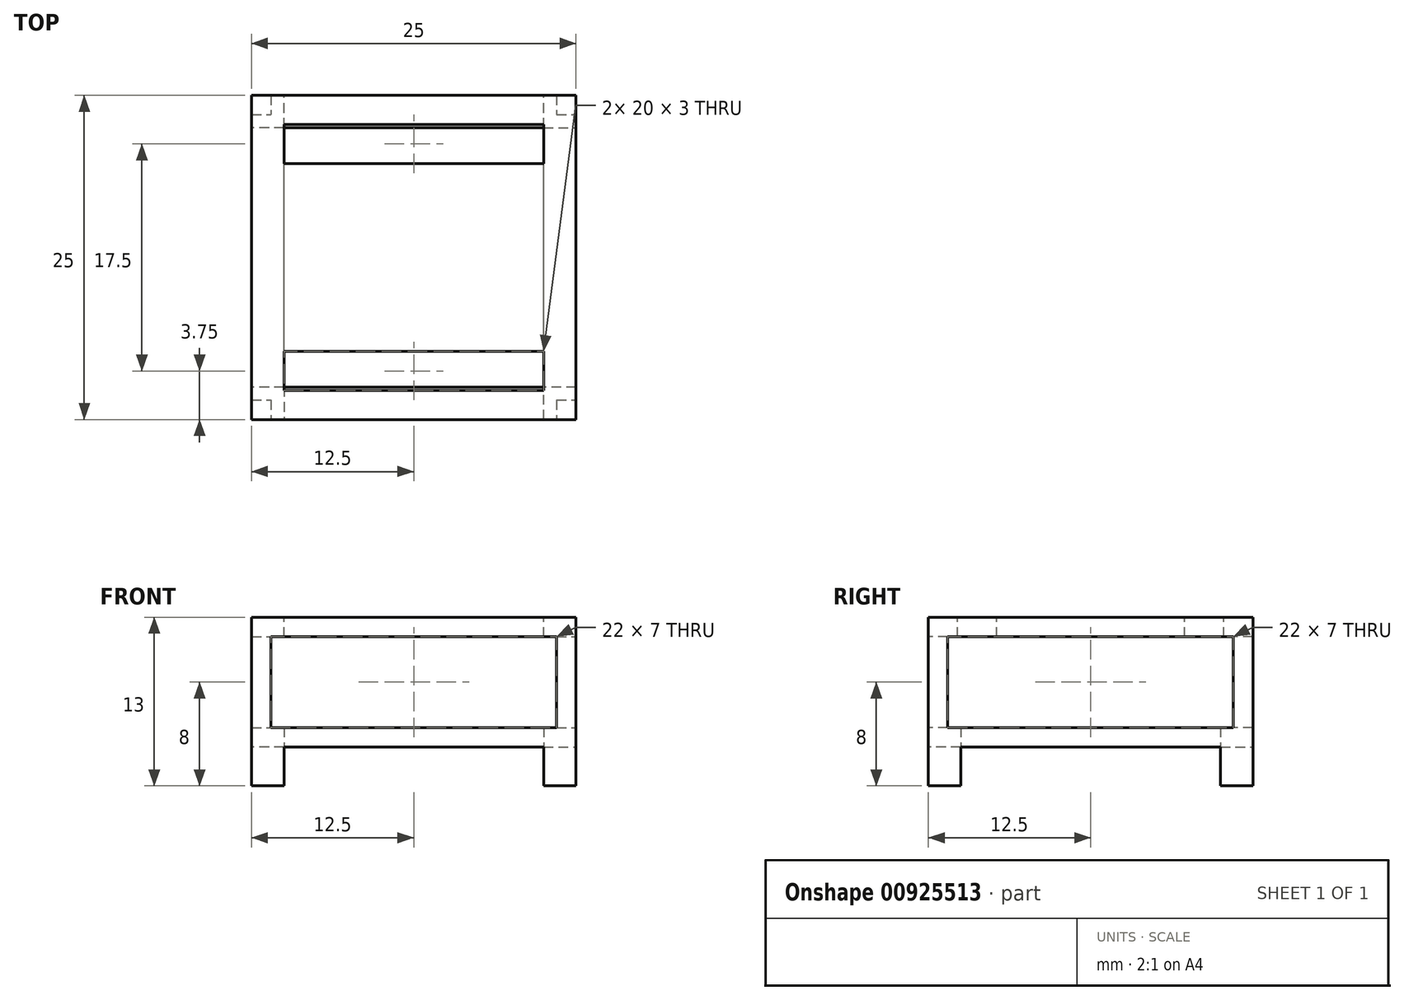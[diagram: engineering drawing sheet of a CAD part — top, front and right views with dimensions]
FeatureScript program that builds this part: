
annotation { "Feature Type Name" : "Feature", "Feature Type Description" : "" }
export const myFeature = defineFeature(function(context is Context, id is Id, definition is map)
    precondition{}
    {
        {
            var Q0;
            Q0=qCreatedBy(makeId("Top.planeOp"),FACE);
            var sketch = newSketch(context, id + "F0", { "sketchPlane" : qUnion([Q0])});
            skLineSegment(sketch, "E0.bottom", {"start": v(-12.5, 12.5) * mm, "end": v(12.5, 12.5) * mm});
            skLineSegment(sketch, "E0.top", {"start": v(-12.5, -12.5) * mm, "end": v(12.5, -12.5) * mm});
            skLineSegment(sketch, "E0.left", {"start": v(-12.5, 12.5) * mm, "end": v(-12.5, -12.5) * mm});
            skLineSegment(sketch, "E0.right", {"start": v(12.5, 12.5) * mm, "end": v(12.5, -12.5) * mm});
            skPoint(sketch, "E0.middle", {"position": v(0, 0) * mm});
            skSolve(sketch);
        }
        {
            var Q0;
            Q0=makeQuery(id+"F0.imprint","IMPRINT",FACE,{"disambiguationData":[TD([[makeQuery(id+"F0.imprint","IMPRINT",EDGE,{"derivedFrom":sQuery(id+"F0.wireOp",EDGE,"E0.bottom")}),-1.0]])]});
            extrude(context, id + "F1", {"entities" : qUnion([Q0]), "depth" : 10 * mm, "offsetDistance" : 25 * mm});
        }
        {
            var Q0;
            Q0=makeQuery(id+"F1.opExtrude","CAP_FACE",FACE,{"disambiguationData":[OSD([sQuery(id+"F0.wireOp",EDGE,"E0.bottom"),sQuery(id+"F0.wireOp",EDGE,"E0.top"),sQuery(id+"F0.wireOp",EDGE,"E0.left"),sQuery(id+"F0.wireOp",EDGE,"E0.right")])],"isStart":false});
            var sketch = newSketch(context, id + "F2", { "sketchPlane" : qUnion([Q0])});
            skCircle(sketch, "E1", {"center": v(0, 0) * mm, "radius": 5 * mm});
            skSolve(sketch);
        }
        {
            var Q0;
            Q0=makeQuery(id+"F2.imprint","IMPRINT",FACE,{"disambiguationData":[TD([[makeQuery(id+"F2.imprint","IMPRINT",EDGE,{"derivedFrom":sQuery(id+"F2.wireOp",EDGE,"E1")}),-1.0]])]});
            var sketch = newSketch(context, id + "F3", { "sketchPlane" : qUnion([Q0])});
            skLineSegment(sketch, "E2", {"start": v(-12.61, 0) * mm, "end": v(12.61, 0) * mm, "construction": true});
            skLineSegment(sketch, "E3", {"start": v(-12.5, -5) * mm, "end": v(12.5, -5) * mm});
            skLineSegment(sketch, "E4.MirrorCS", {"start": v(-12.5, 5) * mm, "end": v(12.5, 5) * mm});
            skPoint(sketch, "E5", {"position": v(0, -8.75) * mm});
            skPoint(sketch, "E6", {"position": v(0, 8.75) * mm});
            skPoint(sketch, "E7", {"position": v(0, 5) * mm});
            skPoint(sketch, "E8", {"position": v(0, -5) * mm});
            skLineSegment(sketch, "E9.bottom", {"start": v(-10, -7.25) * mm, "end": v(10, -7.25) * mm});
            skLineSegment(sketch, "E9.top", {"start": v(-10, -10.25) * mm, "end": v(10, -10.25) * mm});
            skLineSegment(sketch, "E9.left", {"start": v(-10, -7.25) * mm, "end": v(-10, -10.25) * mm});
            skLineSegment(sketch, "E9.right", {"start": v(10, -7.25) * mm, "end": v(10, -10.25) * mm});
            skLineSegment(sketch, "E10.bottom", {"start": v(-10, 10.25) * mm, "end": v(10, 10.25) * mm});
            skLineSegment(sketch, "E10.top", {"start": v(-10, 7.25) * mm, "end": v(10, 7.25) * mm});
            skLineSegment(sketch, "E10.left", {"start": v(-10, 10.25) * mm, "end": v(-10, 7.25) * mm});
            skLineSegment(sketch, "E10.right", {"start": v(10, 10.25) * mm, "end": v(10, 7.25) * mm});
            skSolve(sketch);
        }
        {
            var Q0;
            Q0=makeQuery(id+"F1.opExtrude","SWEPT_FACE",FACE,{"disambiguationData":[OSD([sQuery(id+"F0.wireOp",EDGE,"E0.top")])]});
            var sketch = newSketch(context, id + "F4", { "sketchPlane" : qUnion([Q0])});
            skSolve(sketch);
        }
        {
            var Q0;
            {var subQ0=sQuery(id+"F0.wireOp",EDGE,"E0.top");Q0=makeQuery(id+"F4.imprint","IMPRINT",FACE,{"disambiguationData":[TD([[makeQuery(id+"F4.imprint","IMPRINT",EDGE,{"derivedFrom":makeQuery(id+"F1.opExtrude","CAP_EDGE",EDGE,{"disambiguationData":[OSD([subQ0])],"isStart":true})}),1.0]])]});}
            var sketch = newSketch(context, id + "F5", { "sketchPlane" : qUnion([Q0])});
            skPoint(sketch, "E11", {"position": v(0, 5) * mm});
            skLineSegment(sketch, "E12.bottom", {"start": v(-11, 8.5) * mm, "end": v(11, 8.5) * mm});
            skLineSegment(sketch, "E12.top", {"start": v(-11, 1.5) * mm, "end": v(11, 1.5) * mm});
            skLineSegment(sketch, "E12.left", {"start": v(-11, 8.5) * mm, "end": v(-11, 1.5) * mm});
            skLineSegment(sketch, "E12.right", {"start": v(11, 8.5) * mm, "end": v(11, 1.5) * mm});
            skSolve(sketch);
        }
        {
            var Q0;
            Q0=makeQuery(id+"F5.imprint","IMPRINT",FACE,{"disambiguationData":[TD([[makeQuery(id+"F5.imprint","IMPRINT",EDGE,{"derivedFrom":sQuery(id+"F5.wireOp",EDGE,"E12.bottom")}),-1.0]])]});
            extrude(context, id + "F6", {"entities" : qUnion([Q0]), "operationType" : NewBodyOperationType.REMOVE, "oppositeDirection" : true, "depth" : 25 * mm, "offsetDistance" : 25 * mm});
        }
        {
            var Q0;
            Q0=makeQuery(id+"F1.opExtrude","SWEPT_FACE",FACE,{"disambiguationData":[OSD([sQuery(id+"F0.wireOp",EDGE,"E0.right")])]});
            var sketch = newSketch(context, id + "F7", { "sketchPlane" : qUnion([Q0])});
            skPoint(sketch, "E13", {"position": v(0, 0) * mm});
            skPoint(sketch, "E14", {"position": v(0, 5) * mm});
            skLineSegment(sketch, "E15.bottom", {"start": v(-11, 8.5) * mm, "end": v(11, 8.5) * mm});
            skLineSegment(sketch, "E15.top", {"start": v(-11, 1.5) * mm, "end": v(11, 1.5) * mm});
            skLineSegment(sketch, "E15.left", {"start": v(-11, 8.5) * mm, "end": v(-11, 1.5) * mm});
            skLineSegment(sketch, "E15.right", {"start": v(11, 8.5) * mm, "end": v(11, 1.5) * mm});
            skSolve(sketch);
        }
        {
            var Q0;
            Q0 = qSketchRegion(id + "F7", true);
            extrude(context, id + "F8", {"entities" : qUnion([Q0]), "operationType" : NewBodyOperationType.REMOVE, "oppositeDirection" : true, "depth" : 25 * mm, "offsetDistance" : 25 * mm});
        }
        {
            var Q0;
            Q0=makeQuery(id+"F1.opExtrude","CAP_FACE",FACE,{"disambiguationData":[OSD([sQuery(id+"F0.wireOp",EDGE,"E0.bottom"),sQuery(id+"F0.wireOp",EDGE,"E0.top"),sQuery(id+"F0.wireOp",EDGE,"E0.left"),sQuery(id+"F0.wireOp",EDGE,"E0.right")])],"isStart":true});
            var sketch = newSketch(context, id + "F9", { "sketchPlane" : qUnion([Q0])});
            skLineSegment(sketch, "E16.bottom", {"start": v(-10, 10) * mm, "end": v(10, 10) * mm});
            skLineSegment(sketch, "E16.top", {"start": v(-10, -10) * mm, "end": v(10, -10) * mm});
            skLineSegment(sketch, "E16.left", {"start": v(-10, 10) * mm, "end": v(-10, -10) * mm});
            skLineSegment(sketch, "E16.right", {"start": v(10, 10) * mm, "end": v(10, -10) * mm});
            skPoint(sketch, "E16.middle", {"position": v(0, 0) * mm});
            skSolve(sketch);
        }
        {
            var Q0;
            Q0=makeQuery(id+"F9.imprint","IMPRINT",FACE,{"disambiguationData":[TD([[makeQuery(id+"F9.imprint","IMPRINT",EDGE,{"derivedFrom":sQuery(id+"F9.wireOp",EDGE,"E16.bottom")}),-1.0]])]});
            extrude(context, id + "F10", {"entities" : qUnion([Q0]), "operationType" : NewBodyOperationType.REMOVE, "oppositeDirection" : true, "depth" : 5 * mm, "offsetDistance" : 25 * mm});
        }
        {
            var Q0;
            Q0=makeQuery(id+"F1.opExtrude","CAP_FACE",FACE,{"disambiguationData":[OSD([sQuery(id+"F0.wireOp",EDGE,"E0.bottom"),sQuery(id+"F0.wireOp",EDGE,"E0.top"),sQuery(id+"F0.wireOp",EDGE,"E0.left"),sQuery(id+"F0.wireOp",EDGE,"E0.right")])],"isStart":true});
            var sketch = newSketch(context, id + "F11", { "sketchPlane" : qUnion([Q0])});
            skLineSegment(sketch, "E17.bottom", {"start": v(12.5, 12.5) * mm, "end": v(10, 12.5) * mm});
            skLineSegment(sketch, "E17.top", {"start": v(12.5, 10) * mm, "end": v(10, 10) * mm});
            skLineSegment(sketch, "E17.left", {"start": v(12.5, 12.5) * mm, "end": v(12.5, 10) * mm});
            skLineSegment(sketch, "E17.right", {"start": v(10, 12.5) * mm, "end": v(10, 10) * mm});
            skLineSegment(sketch, "E18.bottom", {"start": v(10, -10) * mm, "end": v(12.5, -10) * mm});
            skLineSegment(sketch, "E18.top", {"start": v(10, -12.5) * mm, "end": v(12.5, -12.5) * mm});
            skLineSegment(sketch, "E18.left", {"start": v(10, -10) * mm, "end": v(10, -12.5) * mm});
            skLineSegment(sketch, "E18.right", {"start": v(12.5, -10) * mm, "end": v(12.5, -12.5) * mm});
            skLineSegment(sketch, "E19.bottom", {"start": v(-10, -10) * mm, "end": v(-12.5, -10) * mm});
            skLineSegment(sketch, "E19.top", {"start": v(-10, -12.5) * mm, "end": v(-12.5, -12.5) * mm});
            skLineSegment(sketch, "E19.left", {"start": v(-10, -10) * mm, "end": v(-10, -12.5) * mm});
            skLineSegment(sketch, "E19.right", {"start": v(-12.5, -10) * mm, "end": v(-12.5, -12.5) * mm});
            skLineSegment(sketch, "E20.bottom", {"start": v(-10, 10) * mm, "end": v(-12.5, 10) * mm});
            skLineSegment(sketch, "E20.top", {"start": v(-10, 12.5) * mm, "end": v(-12.5, 12.5) * mm});
            skLineSegment(sketch, "E20.left", {"start": v(-10, 10) * mm, "end": v(-10, 12.5) * mm});
            skLineSegment(sketch, "E20.right", {"start": v(-12.5, 10) * mm, "end": v(-12.5, 12.5) * mm});
            skSolve(sketch);
        }
        {
            var Q0;
            Q0=makeQuery(id+"F11.imprint","IMPRINT",FACE,{"disambiguationData":[TD([[makeQuery(id+"F11.imprint","IMPRINT",EDGE,{"derivedFrom":sQuery(id+"F11.wireOp",EDGE,"E17.bottom")}),-1.0]])]});
            var Q1;
            Q1=makeQuery(id+"F11.imprint","IMPRINT",FACE,{"disambiguationData":[TD([[makeQuery(id+"F11.imprint","IMPRINT",EDGE,{"derivedFrom":sQuery(id+"F11.wireOp",EDGE,"E20.bottom")}),-1.0]])]});
            var Q2;
            Q2=makeQuery(id+"F11.imprint","IMPRINT",FACE,{"disambiguationData":[TD([[makeQuery(id+"F11.imprint","IMPRINT",EDGE,{"derivedFrom":sQuery(id+"F11.wireOp",EDGE,"E19.bottom")}),1.0]])]});
            var Q3;
            Q3=makeQuery(id+"F11.imprint","IMPRINT",FACE,{"disambiguationData":[TD([[makeQuery(id+"F11.imprint","IMPRINT",EDGE,{"derivedFrom":sQuery(id+"F11.wireOp",EDGE,"E18.bottom")}),-1.0]])]});
            extrude(context, id + "F12", {"entities" : qUnion([Q0, Q1, Q2, Q3]), "operationType" : NewBodyOperationType.ADD, "depth" : 3 * mm, "offsetDistance" : 25 * mm});
        }
        {
            var Q0;
            Q0=makeQuery(id+"F3.imprint","IMPRINT",FACE,{"disambiguationData":[TD([[makeQuery(id+"F3.imprint","IMPRINT",EDGE,{"derivedFrom":sQuery(id+"F3.wireOp",EDGE,"E9.bottom")}),-1.0]])]});
            var Q1;
            Q1=makeQuery(id+"F3.imprint","IMPRINT",FACE,{"disambiguationData":[TD([[makeQuery(id+"F3.imprint","IMPRINT",EDGE,{"derivedFrom":sQuery(id+"F3.wireOp",EDGE,"E10.bottom")}),-1.0]])]});
            extrude(context, id + "F13", {"entities" : qUnion([Q0, Q1]), "operationType" : NewBodyOperationType.REMOVE, "oppositeDirection" : true, "depth" : 5 * mm, "offsetDistance" : 25 * mm});
        }
    });
